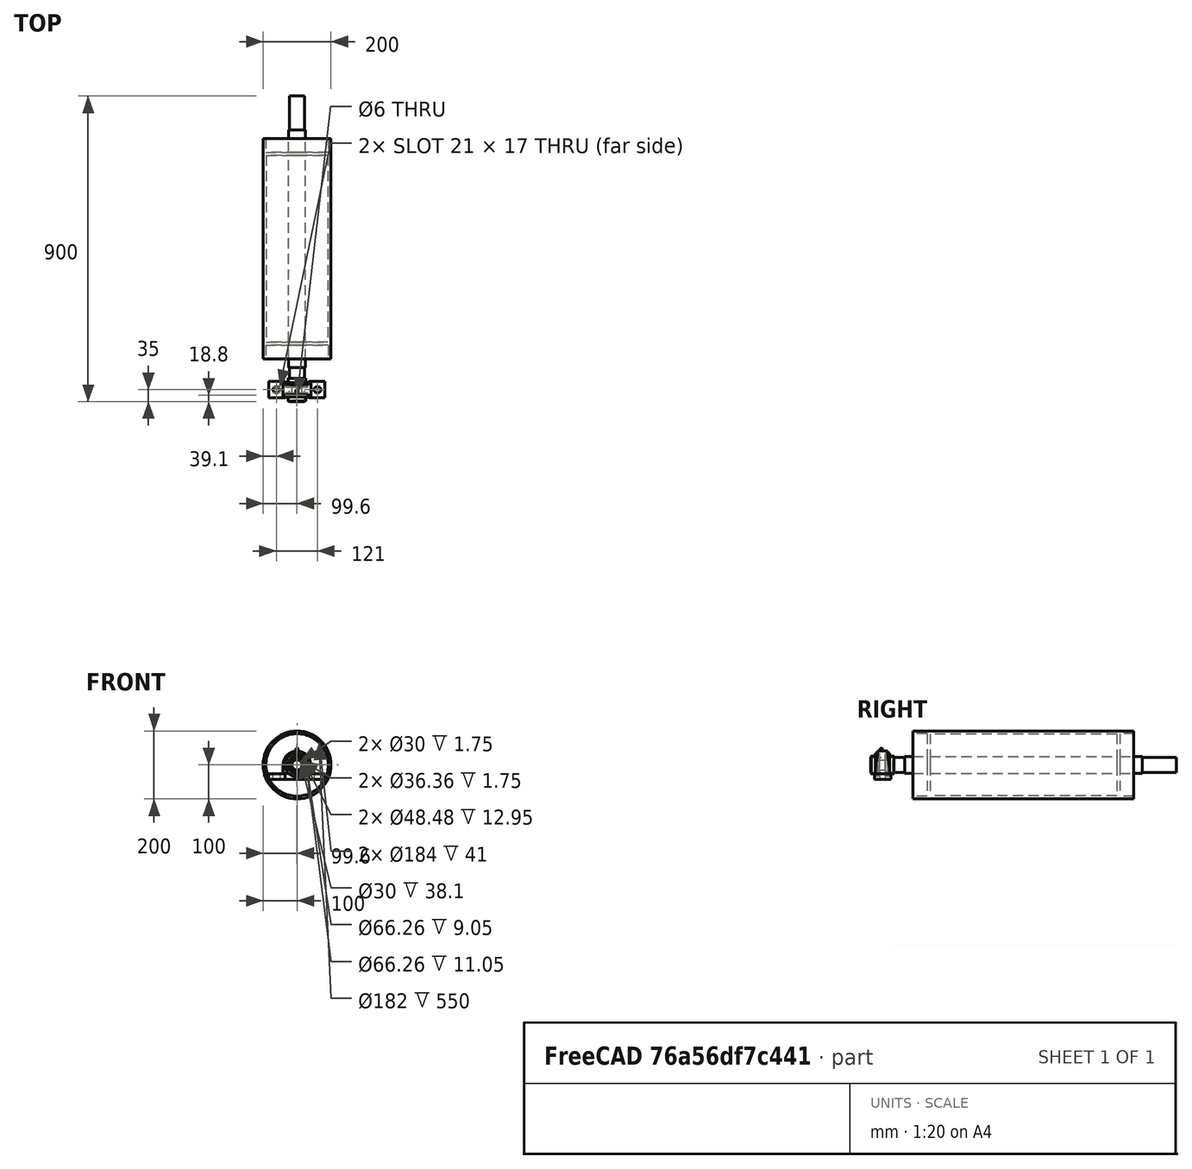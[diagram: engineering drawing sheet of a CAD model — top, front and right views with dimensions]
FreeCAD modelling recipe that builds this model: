
FCSTD DOCUMENT  (FreeCAD 1.0R39319 (Git))
Label: BendPulleyAssy
License: All rights reserved
objects: Part::FeaturePython×2, Part::Feature×1, App::Part×1
note: 3 computed .brp shape members not serialized (recipe doc carries the construction recipe); baked Part::Feature solids carry a one-line shape summary decoded from their .brp

FEATURE [Part::Feature] Part__Feature  label="UCP206FC"
  Placement = pos=(-0.4,415,1.067e-13) rot=(1,0,0;1.5708rad)
  shape: bbox 165 x 70 x 92.1 mm, 127 faces (baked)
  expr: .Placement.Base.y = BendPulley001.L / 2 + 90
FEATURE [Part::FeaturePython] Clone  label="UCP206FC001"  # Draft clone (typed FeaturePython)
  AttacherType = Attacher::AttachEngine3D
  Fuse = false
  Objects = -> [Part__Feature]
  Placement = pos=(-0.4,-415,1.067e-13) rot=(1,0,0;1.5708rad)
  Scale = (1,1,1)
  expr: .Placement.Base.y = -(BendPulley001.L / 2 + 90)
FEATURE [Part::FeaturePython] BendPulley001  label="BendPulley"  # WARN: FeaturePython — macro-defined, semantics opaque (R4)
  BeltWidth = 3
  D = 200
  E = 0
  L = 650
  Placement = pos=(0,0,0) rot=(0,0,1;1.5708rad)
  d1 = 50
  d2 = 45
  d3 = 0
FEATURE [App::Part] Part  label="BendPulleyAssy"
  Group = -> [Part__Feature,Clone,BendPulley001]
  JPN = ベンドプーリ
  Origin = -> Origin
  count = 1
  g0 = 7.85
  mass = 42.6415
